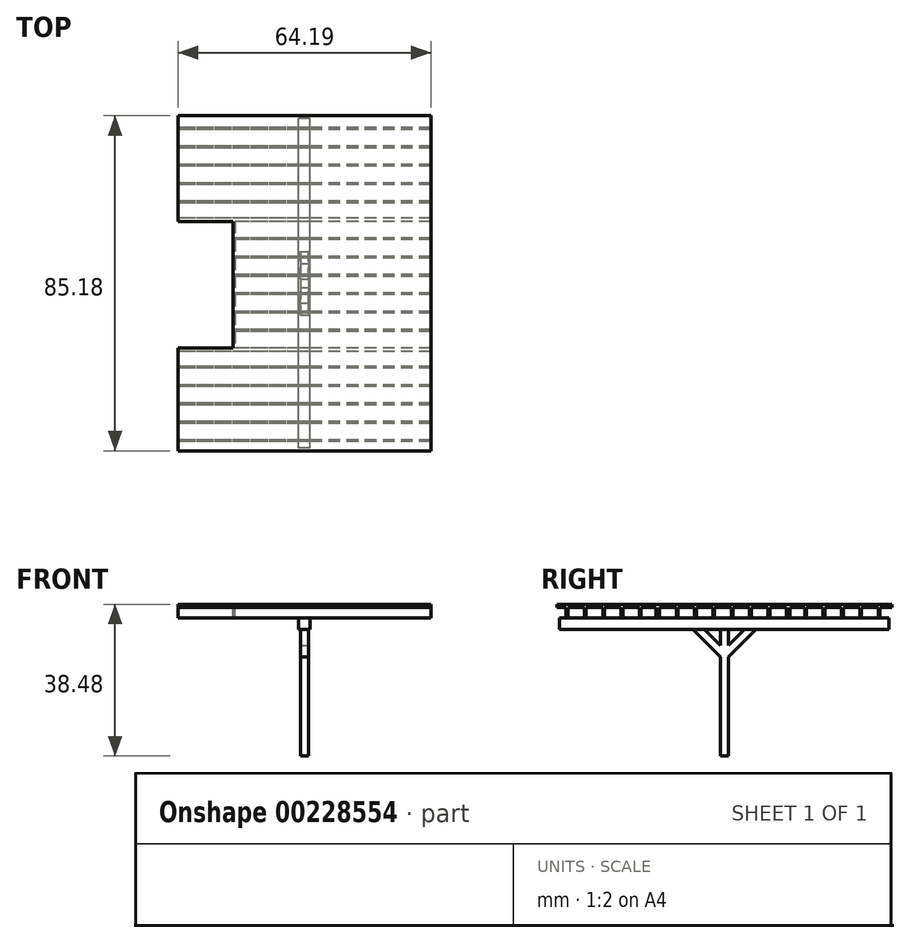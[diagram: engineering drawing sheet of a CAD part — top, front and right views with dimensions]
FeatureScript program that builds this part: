
annotation { "Feature Type Name" : "Feature", "Feature Type Description" : "" }
export const myFeature = defineFeature(function(context is Context, id is Id, definition is map)
    precondition{}
    {
        {
            var Q0;
            Q0=qCreatedBy(makeId("Top.planeOp"),FACE);
            var sketch = newSketch(context, id + "F0", { "sketchPlane" : qUnion([Q0])});
            skLineSegment(sketch, "E0.bottom", {"start": v(-4.2, 0) * mm, "end": v(5863.2, 0) * mm});
            skLineSegment(sketch, "E0.top", {"start": v(-4.2, -7696.2) * mm, "end": v(5863.2, -7696.2) * mm});
            skLineSegment(sketch, "E0.left", {"start": v(-4.2, 0) * mm, "end": v(-4.2, -7696.2) * mm});
            skLineSegment(sketch, "E0.right", {"start": v(5863.2, 0) * mm, "end": v(5863.2, -7696.2) * mm});
            skSolve(sketch);
        }
        {
            var Q0;
            Q0=makeQuery(id+"F0.imprint","IMPRINT",FACE,{"disambiguationData":[TD([[makeQuery(id+"F0.imprint","IMPRINT",EDGE,{"derivedFrom":sQuery(id+"F0.wireOp",EDGE,"E0.bottom")}),-1.0]])]});
            extrude(context, id + "F1", {"entities" : qUnion([Q0]), "depth" : 69.14 * mm});
        }
        {
            var Q0;
            Q0=makeQuery(id+"F1.opExtrude","CAP_FACE",FACE,{"disambiguationData":[OSD([sQuery(id+"F0.wireOp",EDGE,"E0.bottom"),sQuery(id+"F0.wireOp",EDGE,"E0.top"),sQuery(id+"F0.wireOp",EDGE,"E0.left"),sQuery(id+"F0.wireOp",EDGE,"E0.right")])],"isStart":true});
            var sketch = newSketch(context, id + "F2", { "sketchPlane" : qUnion([Q0])});
            skLineSegment(sketch, "E1.0", {"start": v(33.9, 7658.1) * mm, "end": v(5825.1, 7658.1) * mm});
            skLineSegment(sketch, "E1.1", {"start": v(33.9, 38.1) * mm, "end": v(33.9, 7658.1) * mm});
            skLineSegment(sketch, "E1.2", {"start": v(33.9, 38.1) * mm, "end": v(5825.1, 38.1) * mm});
            skLineSegment(sketch, "E1.3", {"start": v(5825.1, 38.1) * mm, "end": v(5825.1, 7658.1) * mm});
            skSolve(sketch);
        }
        {
            var Q0;
            Q0=makeQuery(id+"F2.imprint","IMPRINT",FACE,{"disambiguationData":[TD([[makeQuery(id+"F2.imprint","IMPRINT",EDGE,{"derivedFrom":sQuery(id+"F2.wireOp",EDGE,"E1.0")}),1.0]])]});
            extrude(context, id + "F3", {"entities" : qUnion([Q0]), "operationType" : NewBodyOperationType.ADD, "depth" : 234.95 * mm});
        }
        {
            var Q0;
            Q0=qCreatedBy(makeId("Right.planeOp"),FACE);
            var sketch = newSketch(context, id + "F4", { "sketchPlane" : qUnion([Q0])});
            skLineSegment(sketch, "E2.bottom", {"start": v(-406.4, 0) * mm, "end": v(-444.5, 0) * mm});
            skLineSegment(sketch, "E2.top", {"start": v(-406.4, -234.95) * mm, "end": v(-444.5, -234.95) * mm});
            skLineSegment(sketch, "E2.left", {"start": v(-406.4, 0) * mm, "end": v(-406.4, -234.95) * mm});
            skLineSegment(sketch, "E2.right", {"start": v(-444.5, 0) * mm, "end": v(-444.5, -234.95) * mm});
            skLineSegment(sketch, "E3.1.0.0", {"start": v(-812.8, 0) * mm, "end": v(-812.8, -234.95) * mm});
            skLineSegment(sketch, "E3.1.0.1", {"start": v(-850.9, 0) * mm, "end": v(-850.9, -234.95) * mm});
            skLineSegment(sketch, "E3.1.0.2", {"start": v(-812.8, 0) * mm, "end": v(-850.9, 0) * mm});
            skLineSegment(sketch, "E3.1.0.3", {"start": v(-812.8, -234.95) * mm, "end": v(-850.9, -234.95) * mm});
            skLineSegment(sketch, "E3.2.0.0", {"start": v(-1219.2, 0) * mm, "end": v(-1219.2, -234.95) * mm});
            skLineSegment(sketch, "E3.2.0.1", {"start": v(-1257.3, 0) * mm, "end": v(-1257.3, -234.95) * mm});
            skLineSegment(sketch, "E3.2.0.2", {"start": v(-1219.2, 0) * mm, "end": v(-1257.3, 0) * mm});
            skLineSegment(sketch, "E3.2.0.3", {"start": v(-1219.2, -234.95) * mm, "end": v(-1257.3, -234.95) * mm});
            skLineSegment(sketch, "E3.3.0.0", {"start": v(-1625.6, 0) * mm, "end": v(-1625.6, -234.95) * mm});
            skLineSegment(sketch, "E3.3.0.1", {"start": v(-1663.7, 0) * mm, "end": v(-1663.7, -234.95) * mm});
            skLineSegment(sketch, "E3.3.0.2", {"start": v(-1625.6, 0) * mm, "end": v(-1663.7, 0) * mm});
            skLineSegment(sketch, "E3.3.0.3", {"start": v(-1625.6, -234.95) * mm, "end": v(-1663.7, -234.95) * mm});
            skLineSegment(sketch, "E3.4.0.0", {"start": v(-2032, 0) * mm, "end": v(-2032, -234.95) * mm});
            skLineSegment(sketch, "E3.4.0.1", {"start": v(-2070.1, 0) * mm, "end": v(-2070.1, -234.95) * mm});
            skLineSegment(sketch, "E3.4.0.2", {"start": v(-2032, 0) * mm, "end": v(-2070.1, 0) * mm});
            skLineSegment(sketch, "E3.4.0.3", {"start": v(-2032, -234.95) * mm, "end": v(-2070.1, -234.95) * mm});
            skLineSegment(sketch, "E3.5.0.0", {"start": v(-2438.4, 0) * mm, "end": v(-2438.4, -234.95) * mm});
            skLineSegment(sketch, "E3.5.0.1", {"start": v(-2476.5, 0) * mm, "end": v(-2476.5, -234.95) * mm});
            skLineSegment(sketch, "E3.5.0.2", {"start": v(-2438.4, 0) * mm, "end": v(-2476.5, 0) * mm});
            skLineSegment(sketch, "E3.5.0.3", {"start": v(-2438.4, -234.95) * mm, "end": v(-2476.5, -234.95) * mm});
            skLineSegment(sketch, "E3.6.0.0", {"start": v(-2844.8, 0) * mm, "end": v(-2844.8, -234.95) * mm});
            skLineSegment(sketch, "E3.6.0.1", {"start": v(-2882.9, 0) * mm, "end": v(-2882.9, -234.95) * mm});
            skLineSegment(sketch, "E3.6.0.2", {"start": v(-2844.8, 0) * mm, "end": v(-2882.9, 0) * mm});
            skLineSegment(sketch, "E3.6.0.3", {"start": v(-2844.8, -234.95) * mm, "end": v(-2882.9, -234.95) * mm});
            skLineSegment(sketch, "E3.7.0.0", {"start": v(-3251.2, 0) * mm, "end": v(-3251.2, -234.95) * mm});
            skLineSegment(sketch, "E3.7.0.1", {"start": v(-3289.3, 0) * mm, "end": v(-3289.3, -234.95) * mm});
            skLineSegment(sketch, "E3.7.0.2", {"start": v(-3251.2, 0) * mm, "end": v(-3289.3, 0) * mm});
            skLineSegment(sketch, "E3.7.0.3", {"start": v(-3251.2, -234.95) * mm, "end": v(-3289.3, -234.95) * mm});
            skLineSegment(sketch, "E3.8.0.0", {"start": v(-3657.6, 0) * mm, "end": v(-3657.6, -234.95) * mm});
            skLineSegment(sketch, "E3.8.0.1", {"start": v(-3695.7, 0) * mm, "end": v(-3695.7, -234.95) * mm});
            skLineSegment(sketch, "E3.8.0.2", {"start": v(-3657.6, 0) * mm, "end": v(-3695.7, 0) * mm});
            skLineSegment(sketch, "E3.8.0.3", {"start": v(-3657.6, -234.95) * mm, "end": v(-3695.7, -234.95) * mm});
            skLineSegment(sketch, "E3.9.0.0", {"start": v(-4064, 0) * mm, "end": v(-4064, -234.95) * mm});
            skLineSegment(sketch, "E3.9.0.1", {"start": v(-4102.1, 0) * mm, "end": v(-4102.1, -234.95) * mm});
            skLineSegment(sketch, "E3.9.0.2", {"start": v(-4064, 0) * mm, "end": v(-4102.1, 0) * mm});
            skLineSegment(sketch, "E3.9.0.3", {"start": v(-4064, -234.95) * mm, "end": v(-4102.1, -234.95) * mm});
            skLineSegment(sketch, "E3.10.0.0", {"start": v(-4470.4, 0) * mm, "end": v(-4470.4, -234.95) * mm});
            skLineSegment(sketch, "E3.10.0.1", {"start": v(-4508.5, 0) * mm, "end": v(-4508.5, -234.95) * mm});
            skLineSegment(sketch, "E3.10.0.2", {"start": v(-4470.4, 0) * mm, "end": v(-4508.5, 0) * mm});
            skLineSegment(sketch, "E3.10.0.3", {"start": v(-4470.4, -234.95) * mm, "end": v(-4508.5, -234.95) * mm});
            skLineSegment(sketch, "E3.11.0.0", {"start": v(-4876.8, 0) * mm, "end": v(-4876.8, -234.95) * mm});
            skLineSegment(sketch, "E3.11.0.1", {"start": v(-4914.9, 0) * mm, "end": v(-4914.9, -234.95) * mm});
            skLineSegment(sketch, "E3.11.0.2", {"start": v(-4876.8, 0) * mm, "end": v(-4914.9, 0) * mm});
            skLineSegment(sketch, "E3.11.0.3", {"start": v(-4876.8, -234.95) * mm, "end": v(-4914.9, -234.95) * mm});
            skLineSegment(sketch, "E3.12.0.0", {"start": v(-5283.2, 0) * mm, "end": v(-5283.2, -234.95) * mm});
            skLineSegment(sketch, "E3.12.0.1", {"start": v(-5321.3, 0) * mm, "end": v(-5321.3, -234.95) * mm});
            skLineSegment(sketch, "E3.12.0.2", {"start": v(-5283.2, 0) * mm, "end": v(-5321.3, 0) * mm});
            skLineSegment(sketch, "E3.12.0.3", {"start": v(-5283.2, -234.95) * mm, "end": v(-5321.3, -234.95) * mm});
            skLineSegment(sketch, "E3.13.0.0", {"start": v(-5689.6, 0) * mm, "end": v(-5689.6, -234.95) * mm});
            skLineSegment(sketch, "E3.13.0.1", {"start": v(-5727.7, 0) * mm, "end": v(-5727.7, -234.95) * mm});
            skLineSegment(sketch, "E3.13.0.2", {"start": v(-5689.6, 0) * mm, "end": v(-5727.7, 0) * mm});
            skLineSegment(sketch, "E3.13.0.3", {"start": v(-5689.6, -234.95) * mm, "end": v(-5727.7, -234.95) * mm});
            skLineSegment(sketch, "E3.14.0.0", {"start": v(-6096, 0) * mm, "end": v(-6096, -234.95) * mm});
            skLineSegment(sketch, "E3.14.0.1", {"start": v(-6134.1, 0) * mm, "end": v(-6134.1, -234.95) * mm});
            skLineSegment(sketch, "E3.14.0.2", {"start": v(-6096, 0) * mm, "end": v(-6134.1, 0) * mm});
            skLineSegment(sketch, "E3.14.0.3", {"start": v(-6096, -234.95) * mm, "end": v(-6134.1, -234.95) * mm});
            skLineSegment(sketch, "E3.15.0.0", {"start": v(-6502.4, 0) * mm, "end": v(-6502.4, -234.95) * mm});
            skLineSegment(sketch, "E3.15.0.1", {"start": v(-6540.5, 0) * mm, "end": v(-6540.5, -234.95) * mm});
            skLineSegment(sketch, "E3.15.0.2", {"start": v(-6502.4, 0) * mm, "end": v(-6540.5, 0) * mm});
            skLineSegment(sketch, "E3.15.0.3", {"start": v(-6502.4, -234.95) * mm, "end": v(-6540.5, -234.95) * mm});
            skLineSegment(sketch, "E3.16.0.0", {"start": v(-6908.8, 0) * mm, "end": v(-6908.8, -234.95) * mm});
            skLineSegment(sketch, "E3.16.0.1", {"start": v(-6946.9, 0) * mm, "end": v(-6946.9, -234.95) * mm});
            skLineSegment(sketch, "E3.16.0.2", {"start": v(-6908.8, 0) * mm, "end": v(-6946.9, 0) * mm});
            skLineSegment(sketch, "E3.16.0.3", {"start": v(-6908.8, -234.95) * mm, "end": v(-6946.9, -234.95) * mm});
            skLineSegment(sketch, "E3.direction1", {"start": v(-444.5, -234.95) * mm, "end": v(-850.9, -234.95) * mm, "construction": true});
            skLineSegment(sketch, "E4.0.17.0", {"start": v(-7315.2, 0) * mm, "end": v(-7315.2, -234.95) * mm});
            skLineSegment(sketch, "E4.3.17.0", {"start": v(-7353.3, 0) * mm, "end": v(-7353.3, -234.95) * mm});
            skLineSegment(sketch, "E4.6.17.0", {"start": v(-7315.2, 0) * mm, "end": v(-7353.3, 0) * mm});
            skLineSegment(sketch, "E4.9.17.0", {"start": v(-7315.2, -234.95) * mm, "end": v(-7353.3, -234.95) * mm});
            skSolve(sketch);
        }
        {
            var Q0;
            Q0=makeQuery(id+"F4.imprint","IMPRINT",FACE,{"disambiguationData":[TD([[makeQuery(id+"F4.imprint","IMPRINT",EDGE,{"derivedFrom":sQuery(id+"F4.wireOp",EDGE,"E2.bottom")}),1.0]])]});
            var Q1;
            Q1=makeQuery(id+"F4.imprint","IMPRINT",FACE,{"disambiguationData":[TD([[makeQuery(id+"F4.imprint","IMPRINT",EDGE,{"derivedFrom":sQuery(id+"F4.wireOp",EDGE,"E3.1.0.0")}),-1.0]])]});
            var Q2;
            Q2=makeQuery(id+"F4.imprint","IMPRINT",FACE,{"disambiguationData":[TD([[makeQuery(id+"F4.imprint","IMPRINT",EDGE,{"derivedFrom":sQuery(id+"F4.wireOp",EDGE,"E3.2.0.0")}),-1.0]])]});
            var Q3;
            Q3=makeQuery(id+"F4.imprint","IMPRINT",FACE,{"disambiguationData":[TD([[makeQuery(id+"F4.imprint","IMPRINT",EDGE,{"derivedFrom":sQuery(id+"F4.wireOp",EDGE,"E3.3.0.0")}),-1.0]])]});
            var Q4;
            Q4=makeQuery(id+"F4.imprint","IMPRINT",FACE,{"disambiguationData":[TD([[makeQuery(id+"F4.imprint","IMPRINT",EDGE,{"derivedFrom":sQuery(id+"F4.wireOp",EDGE,"E3.4.0.0")}),-1.0]])]});
            var Q5;
            Q5=makeQuery(id+"F4.imprint","IMPRINT",FACE,{"disambiguationData":[TD([[makeQuery(id+"F4.imprint","IMPRINT",EDGE,{"derivedFrom":sQuery(id+"F4.wireOp",EDGE,"E3.5.0.0")}),-1.0]])]});
            var Q6;
            Q6=makeQuery(id+"F4.imprint","IMPRINT",FACE,{"disambiguationData":[TD([[makeQuery(id+"F4.imprint","IMPRINT",EDGE,{"derivedFrom":sQuery(id+"F4.wireOp",EDGE,"E3.6.0.0")}),-1.0]])]});
            var Q7;
            Q7=makeQuery(id+"F4.imprint","IMPRINT",FACE,{"disambiguationData":[TD([[makeQuery(id+"F4.imprint","IMPRINT",EDGE,{"derivedFrom":sQuery(id+"F4.wireOp",EDGE,"E3.7.0.0")}),-1.0]])]});
            var Q8;
            Q8=makeQuery(id+"F4.imprint","IMPRINT",FACE,{"disambiguationData":[TD([[makeQuery(id+"F4.imprint","IMPRINT",EDGE,{"derivedFrom":sQuery(id+"F4.wireOp",EDGE,"E3.8.0.0")}),-1.0]])]});
            var Q9;
            Q9=makeQuery(id+"F4.imprint","IMPRINT",FACE,{"disambiguationData":[TD([[makeQuery(id+"F4.imprint","IMPRINT",EDGE,{"derivedFrom":sQuery(id+"F4.wireOp",EDGE,"E3.9.0.0")}),-1.0]])]});
            var Q10;
            Q10=makeQuery(id+"F4.imprint","IMPRINT",FACE,{"disambiguationData":[TD([[makeQuery(id+"F4.imprint","IMPRINT",EDGE,{"derivedFrom":sQuery(id+"F4.wireOp",EDGE,"E3.10.0.0")}),-1.0]])]});
            var Q11;
            Q11=makeQuery(id+"F4.imprint","IMPRINT",FACE,{"disambiguationData":[TD([[makeQuery(id+"F4.imprint","IMPRINT",EDGE,{"derivedFrom":sQuery(id+"F4.wireOp",EDGE,"E3.11.0.0")}),-1.0]])]});
            var Q12;
            Q12=makeQuery(id+"F4.imprint","IMPRINT",FACE,{"disambiguationData":[TD([[makeQuery(id+"F4.imprint","IMPRINT",EDGE,{"derivedFrom":sQuery(id+"F4.wireOp",EDGE,"E3.12.0.0")}),-1.0]])]});
            var Q13;
            Q13=makeQuery(id+"F4.imprint","IMPRINT",FACE,{"disambiguationData":[TD([[makeQuery(id+"F4.imprint","IMPRINT",EDGE,{"derivedFrom":sQuery(id+"F4.wireOp",EDGE,"E3.13.0.0")}),-1.0]])]});
            var Q14;
            Q14=makeQuery(id+"F4.imprint","IMPRINT",FACE,{"disambiguationData":[TD([[makeQuery(id+"F4.imprint","IMPRINT",EDGE,{"derivedFrom":sQuery(id+"F4.wireOp",EDGE,"E3.14.0.0")}),-1.0]])]});
            var Q15;
            Q15=makeQuery(id+"F4.imprint","IMPRINT",FACE,{"disambiguationData":[TD([[makeQuery(id+"F4.imprint","IMPRINT",EDGE,{"derivedFrom":sQuery(id+"F4.wireOp",EDGE,"E3.15.0.0")}),-1.0]])]});
            var Q16;
            Q16=makeQuery(id+"F4.imprint","IMPRINT",FACE,{"disambiguationData":[TD([[makeQuery(id+"F4.imprint","IMPRINT",EDGE,{"derivedFrom":sQuery(id+"F4.wireOp",EDGE,"E3.16.0.0")}),-1.0]])]});
            var Q17;
            Q17=makeQuery(id+"F4.imprint","IMPRINT",FACE,{"disambiguationData":[TD([[makeQuery(id+"F4.imprint","IMPRINT",EDGE,{"derivedFrom":sQuery(id+"F4.wireOp",EDGE,"E4.0.17.0")}),-1.0]])]});
            var Q18;
            Q18=makeQuery(id+"F1.opExtrude","SWEPT_FACE",FACE,{"disambiguationData":[OSD([sQuery(id+"F0.wireOp",EDGE,"E0.right")])]});
            extrude(context, id + "F5", {"entities" : qUnion([Q0, Q1, Q2, Q3, Q4, Q5, Q6, Q7, Q8, Q9, Q10, Q11, Q12, Q13, Q14, Q15, Q16, Q17]), "operationType" : NewBodyOperationType.ADD, "endBound" : BoundingType.UP_TO_SURFACE, "endBoundEntityFace" : qUnion([Q18]), "depth" : 25.4 * mm});
        }
        {
            var Q0;
            {var subQ0=sQuery(id+"F0.wireOp",EDGE,"E0.bottom");Q0=makeQuery(id+"F3.boolean.opBoolean","MERGE",FACE,{"derivedFrom":[makeQuery(id+"F1.opExtrude","SWEPT_FACE",FACE,{"disambiguationData":[OSD([subQ0])]}),makeQuery(id+"F3.opExtrude","SWEPT_FACE",FACE,{"disambiguationData":[OSD([subQ0])]})]});}
            cPlane(context, id + "F6", {"entities" : qUnion([Q0]), "cplaneType" : CPlaneType.OFFSET, "offset" : 203.2 * mm, "oppositeDirection" : true, "width" : 152.4 * mm, "height" : 152.4 * mm});
        }
        {
            var Q0;
            Q0=qCreatedBy(id+"F6.planeOp",FACE);
            var sketch = newSketch(context, id + "F7", { "sketchPlane" : qUnion([Q0])});
            skLineSegment(sketch, "E5.bottom", {"start": v(-3056.5, -234.95) * mm, "end": v(-2802.5, -234.95) * mm});
            skLineSegment(sketch, "E5.top", {"start": v(-3056.5, -488.95) * mm, "end": v(-2802.5, -488.95) * mm});
            skLineSegment(sketch, "E5.left", {"start": v(-3056.5, -234.95) * mm, "end": v(-3056.5, -488.95) * mm});
            skLineSegment(sketch, "E5.right", {"start": v(-2802.5, -234.95) * mm, "end": v(-2802.5, -488.95) * mm});
            skSolve(sketch);
        }
        {
            var Q0;
            Q0=makeQuery(id+"F7.imprint","IMPRINT",FACE,{"disambiguationData":[TD([[makeQuery(id+"F7.imprint","IMPRINT",EDGE,{"derivedFrom":sQuery(id+"F7.wireOp",EDGE,"E5.bottom")}),-1.0]])]});
            extrude(context, id + "F8", {"entities" : qUnion([Q0]), "operationType" : NewBodyOperationType.ADD, "oppositeDirection" : true, "depth" : 7289.8 * mm});
        }
        {
            var Q0;
            Q0=makeQuery(id+"F8.opExtrude","SWEPT_FACE",FACE,{"disambiguationData":[OSD([sQuery(id+"F7.wireOp",EDGE,"E5.top")])]});
            var sketch = newSketch(context, id + "F9", { "sketchPlane" : qUnion([Q0])});
            skLineSegment(sketch, "E6", {"start": v(2929.5, 7493) * mm, "end": v(2929.5, 203.2) * mm, "construction": true});
            skLineSegment(sketch, "E7", {"start": v(2802.5, 3848.1) * mm, "end": v(3056.5, 3848.1) * mm, "construction": true});
            skLineSegment(sketch, "E8.bottom", {"start": v(3021.58, 3756.03) * mm, "end": v(2837.43, 3756.03) * mm});
            skLineSegment(sketch, "E8.top", {"start": v(3021.58, 3940.18) * mm, "end": v(2837.43, 3940.18) * mm});
            skLineSegment(sketch, "E8.left", {"start": v(3021.58, 3756.03) * mm, "end": v(3021.58, 3940.18) * mm});
            skLineSegment(sketch, "E8.right", {"start": v(2837.43, 3756.03) * mm, "end": v(2837.43, 3940.18) * mm});
            skPoint(sketch, "E8.middle", {"position": v(2929.5, 3848.1) * mm});
            skSolve(sketch);
        }
        {
            var Q0;
            Q0=makeQuery(id+"F9.imprint","IMPRINT",FACE,{"disambiguationData":[TD([[makeQuery(id+"F9.imprint","IMPRINT",EDGE,{"derivedFrom":sQuery(id+"F9.wireOp",EDGE,"E8.bottom")}),-1.0]])]});
            extrude(context, id + "F10", {"entities" : qUnion([Q0]), "operationType" : NewBodyOperationType.ADD, "depth" : 2794 * mm});
        }
        {
            var Q0;
            Q0=makeQuery(id+"F10.opExtrude","SWEPT_FACE",FACE,{"disambiguationData":[OSD([sQuery(id+"F9.wireOp",EDGE,"E8.left")])]});
            var sketch = newSketch(context, id + "F11", { "sketchPlane" : qUnion([Q0])});
            skLineSegment(sketch, "E9", {"start": v(-4289.35, -488.95) * mm, "end": v(-3940.17, -838.12) * mm});
            skLineSegment(sketch, "E10", {"start": v(-3940.17, -838.12) * mm, "end": v(-3940.17, -1098.55) * mm});
            skLineSegment(sketch, "E11", {"start": v(-3940.17, -1098.55) * mm, "end": v(-4549.77, -488.95) * mm});
            skLineSegment(sketch, "E12", {"start": v(-4549.77, -488.95) * mm, "end": v(-4289.35, -488.95) * mm});
            skLineSegment(sketch, "E13", {"start": v(-3848.1, -488.95) * mm, "end": v(-3848.1, -1270.1) * mm, "construction": true});
            skLineSegment(sketch, "E14.MirrorCS", {"start": v(-3146.42, -488.95) * mm, "end": v(-3406.85, -488.95) * mm});
            skLineSegment(sketch, "E15.MirrorCS", {"start": v(-3756.02, -1098.55) * mm, "end": v(-3146.42, -488.95) * mm});
            skLineSegment(sketch, "E16.MirrorCS", {"start": v(-3406.85, -488.95) * mm, "end": v(-3756.02, -838.12) * mm});
            skLineSegment(sketch, "E17.MirrorCS", {"start": v(-3756.02, -838.12) * mm, "end": v(-3756.02, -1098.55) * mm});
            skSolve(sketch);
        }
        {
            var Q0;
            Q0=makeQuery(id+"F11.imprint","IMPRINT",FACE,{"disambiguationData":[TD([[makeQuery(id+"F11.imprint","IMPRINT",EDGE,{"derivedFrom":sQuery(id+"F11.wireOp",EDGE,"E9")}),-1.0]])]});
            var Q1;
            Q1=makeQuery(id+"F11.imprint","IMPRINT",FACE,{"disambiguationData":[TD([[makeQuery(id+"F11.imprint","IMPRINT",EDGE,{"derivedFrom":sQuery(id+"F11.wireOp",EDGE,"E14.MirrorCS")}),1.0]])]});
            var Q2;
            Q2=makeQuery(id+"F10.opExtrude","SWEPT_FACE",FACE,{"disambiguationData":[OSD([sQuery(id+"F9.wireOp",EDGE,"E8.right")])]});
            extrude(context, id + "F12", {"entities" : qUnion([Q0, Q1]), "operationType" : NewBodyOperationType.ADD, "endBound" : BoundingType.UP_TO_SURFACE, "oppositeDirection" : true, "endBoundEntityFace" : qUnion([Q2]), "depth" : 25.4 * mm});
        }
        {
            var Q0;
            Q0=makeQuery(id+"F1.opExtrude","CAP_FACE",FACE,{"disambiguationData":[OSD([sQuery(id+"F0.wireOp",EDGE,"E0.bottom"),sQuery(id+"F0.wireOp",EDGE,"E0.top"),sQuery(id+"F0.wireOp",EDGE,"E0.left"),sQuery(id+"F0.wireOp",EDGE,"E0.right")])],"isStart":false});
            var sketch = newSketch(context, id + "F13", { "sketchPlane" : qUnion([Q0])});
            skLineSegment(sketch, "E18.0", {"start": v(134.08, -138.28) * mm, "end": v(5724.93, -138.28) * mm});
            skLineSegment(sketch, "E18.1", {"start": v(134.08, -138.28) * mm, "end": v(134.08, -7557.92) * mm});
            skLineSegment(sketch, "E18.2", {"start": v(134.08, -7557.92) * mm, "end": v(5724.93, -7557.92) * mm});
            skLineSegment(sketch, "E18.3", {"start": v(5724.93, -138.28) * mm, "end": v(5724.93, -7557.92) * mm});
            skLineSegment(sketch, "E19.0", {"start": v(-4.2, 0) * mm, "end": v(5863.2, 0) * mm});
            skLineSegment(sketch, "E20.0", {"start": v(-4.2, 0) * mm, "end": v(-4.2, -7696.2) * mm});
            skLineSegment(sketch, "E21.0", {"start": v(-4.2, -7696.2) * mm, "end": v(5863.2, -7696.2) * mm});
            skLineSegment(sketch, "E22.0", {"start": v(5863.2, 0) * mm, "end": v(5863.2, -7696.2) * mm});
            skSolve(sketch);
        }
        {
            var Q0;
            Q0=makeQuery(id+"F13.imprint","IMPRINT",FACE,{"disambiguationData":[TD([[makeQuery(id+"F13.imprint","IMPRINT",EDGE,{"derivedFrom":sQuery(id+"F13.wireOp",EDGE,"E18.0")}),1.0]])]});
            var Q1;
            Q1=makeQuery(id+"F5.boolean.opBoolean","MERGE",FACE,{"derivedFrom":[makeQuery(id+"F3.opExtrude","CAP_FACE",FACE,{"disambiguationData":[OSD([sQuery(id+"F0.wireOp",EDGE,"E0.bottom"),sQuery(id+"F0.wireOp",EDGE,"E0.top"),sQuery(id+"F0.wireOp",EDGE,"E0.left"),sQuery(id+"F0.wireOp",EDGE,"E0.right"),sQuery(id+"F2.wireOp",EDGE,"E1.0"),sQuery(id+"F2.wireOp",EDGE,"E1.1"),sQuery(id+"F2.wireOp",EDGE,"E1.2"),sQuery(id+"F2.wireOp",EDGE,"E1.3")])],"isStart":false}),makeQuery(id+"F5.opExtrude","SWEPT_FACE",FACE,{"disambiguationData":[OSD([sQuery(id+"F4.wireOp",EDGE,"E2.top")])]}),makeQuery(id+"F5.opExtrude","SWEPT_FACE",FACE,{"disambiguationData":[OSD([sQuery(id+"F4.wireOp",EDGE,"E3.1.0.3")])]}),makeQuery(id+"F5.opExtrude","SWEPT_FACE",FACE,{"disambiguationData":[OSD([sQuery(id+"F4.wireOp",EDGE,"E3.2.0.3")])]}),makeQuery(id+"F5.opExtrude","SWEPT_FACE",FACE,{"disambiguationData":[OSD([sQuery(id+"F4.wireOp",EDGE,"E3.3.0.3")])]}),makeQuery(id+"F5.opExtrude","SWEPT_FACE",FACE,{"disambiguationData":[OSD([sQuery(id+"F4.wireOp",EDGE,"E3.4.0.3")])]}),makeQuery(id+"F5.opExtrude","SWEPT_FACE",FACE,{"disambiguationData":[OSD([sQuery(id+"F4.wireOp",EDGE,"E3.5.0.3")])]}),makeQuery(id+"F5.opExtrude","SWEPT_FACE",FACE,{"disambiguationData":[OSD([sQuery(id+"F4.wireOp",EDGE,"E3.6.0.3")])]}),makeQuery(id+"F5.opExtrude","SWEPT_FACE",FACE,{"disambiguationData":[OSD([sQuery(id+"F4.wireOp",EDGE,"E3.7.0.3")])]}),makeQuery(id+"F5.opExtrude","SWEPT_FACE",FACE,{"disambiguationData":[OSD([sQuery(id+"F4.wireOp",EDGE,"E3.8.0.3")])]}),makeQuery(id+"F5.opExtrude","SWEPT_FACE",FACE,{"disambiguationData":[OSD([sQuery(id+"F4.wireOp",EDGE,"E3.9.0.3")])]}),makeQuery(id+"F5.opExtrude","SWEPT_FACE",FACE,{"disambiguationData":[OSD([sQuery(id+"F4.wireOp",EDGE,"E3.10.0.3")])]}),makeQuery(id+"F5.opExtrude","SWEPT_FACE",FACE,{"disambiguationData":[OSD([sQuery(id+"F4.wireOp",EDGE,"E3.11.0.3")])]}),makeQuery(id+"F5.opExtrude","SWEPT_FACE",FACE,{"disambiguationData":[OSD([sQuery(id+"F4.wireOp",EDGE,"E3.12.0.3")])]}),makeQuery(id+"F5.opExtrude","SWEPT_FACE",FACE,{"disambiguationData":[OSD([sQuery(id+"F4.wireOp",EDGE,"E3.13.0.3")])]}),makeQuery(id+"F5.opExtrude","SWEPT_FACE",FACE,{"disambiguationData":[OSD([sQuery(id+"F4.wireOp",EDGE,"E3.14.0.3")])]}),makeQuery(id+"F5.opExtrude","SWEPT_FACE",FACE,{"disambiguationData":[OSD([sQuery(id+"F4.wireOp",EDGE,"E3.15.0.3")])]}),makeQuery(id+"F5.opExtrude","SWEPT_FACE",FACE,{"disambiguationData":[OSD([sQuery(id+"F4.wireOp",EDGE,"E3.16.0.3")])]}),makeQuery(id+"F5.opExtrude","SWEPT_FACE",FACE,{"disambiguationData":[OSD([sQuery(id+"F4.wireOp",EDGE,"E4.9.17.0")])]})]});
            extrude(context, id + "F14", {"entities" : qUnion([Q0]), "operationType" : NewBodyOperationType.REMOVE, "endBound" : BoundingType.UP_TO_SURFACE, "oppositeDirection" : true, "endBoundEntityFace" : qUnion([Q1]), "depth" : 25.4 * mm});
        }
        {
            var Q0;
            Q0=makeQuery(id+"F1.opExtrude","CAP_FACE",FACE,{"disambiguationData":[OSD([sQuery(id+"F0.wireOp",EDGE,"E0.bottom"),sQuery(id+"F0.wireOp",EDGE,"E0.top"),sQuery(id+"F0.wireOp",EDGE,"E0.left"),sQuery(id+"F0.wireOp",EDGE,"E0.right")])],"isStart":false});
            var sketch = newSketch(context, id + "F15", { "sketchPlane" : qUnion([Q0])});
            skLineSegment(sketch, "E23.bottom", {"start": v(134.08, -2476.5) * mm, "end": v(1353.28, -2476.5) * mm});
            skLineSegment(sketch, "E23.top", {"start": v(134.08, -5283.2) * mm, "end": v(1353.28, -5283.2) * mm});
            skLineSegment(sketch, "E23.left", {"start": v(134.08, -2476.5) * mm, "end": v(134.08, -5283.2) * mm});
            skLineSegment(sketch, "E23.right", {"start": v(1353.28, -2476.5) * mm, "end": v(1353.28, -5283.2) * mm});
            skSolve(sketch);
        }
        {
            var Q0;
            Q0=makeQuery(id+"F15.imprint","IMPRINT",FACE,{"disambiguationData":[TD([[makeQuery(id+"F15.imprint","IMPRINT",EDGE,{"derivedFrom":sQuery(id+"F15.wireOp",EDGE,"E23.bottom")}),-1.0]])]});
            extrude(context, id + "F16", {"entities" : qUnion([Q0]), "operationType" : NewBodyOperationType.REMOVE, "oppositeDirection" : true, "depth" : 304.8 * mm});
        }
        {
            var Q0;
            Q0=makeQuery(id+"F16.boolean.opBoolean","COPY",FACE,{"derivedFrom":makeQuery(id+"F16.opExtrude","SWEPT_FACE",FACE,{"disambiguationData":[OSD([sQuery(id+"F15.wireOp",EDGE,"E23.right")])]})});
            var sketch = newSketch(context, id + "F17", { "sketchPlane" : qUnion([Q0])});
            skLineSegment(sketch, "E24.bottom", {"start": v(2476.5, 0) * mm, "end": v(5283.2, 0) * mm});
            skLineSegment(sketch, "E24.top", {"start": v(2476.5, -234.95) * mm, "end": v(5283.2, -234.95) * mm});
            skLineSegment(sketch, "E24.left", {"start": v(2476.5, 0) * mm, "end": v(2476.5, -234.95) * mm});
            skLineSegment(sketch, "E24.right", {"start": v(5283.2, 0) * mm, "end": v(5283.2, -234.95) * mm});
            skSolve(sketch);
        }
        {
            var Q0;
            {var subQ0=sQuery(id+"F17.wireOp",EDGE,"E24.left");Q0=makeQuery(id+"F17.imprint","IMPRINT",FACE,{"disambiguationData":[TD([[makeQuery(id+"F17.imprint","IMPRINT",EDGE,{"derivedFrom":subQ0}),1.0]])]});}
            var Q1;
            {var subQ1=makeQuery(id+"F16.opExtrude","SWEPT_FACE",FACE,{"disambiguationData":[OSD([sQuery(id+"F15.wireOp",EDGE,"E23.right")])]});var subQ2=makeQuery(id+"F16.boolean.opBoolean","INTERSECT",EDGE,{"derivedFrom":[makeQuery(id+"F5.opExtrude","SWEPT_FACE",FACE,{"disambiguationData":[OSD([sQuery(id+"F4.wireOp",EDGE,"E3.6.0.1")])]}),subQ1]});Q1=makeQuery(id+"F17.imprint","IMPRINT",FACE,{"disambiguationData":[TD([[makeQuery(id+"F17.imprint","IMPRINT",EDGE,{"derivedFrom":subQ2}),-1.0]])]});}
            var Q2;
            {var subQ1=makeQuery(id+"F16.opExtrude","SWEPT_FACE",FACE,{"disambiguationData":[OSD([sQuery(id+"F15.wireOp",EDGE,"E23.right")])]});var subQ2=makeQuery(id+"F16.boolean.opBoolean","INTERSECT",EDGE,{"derivedFrom":[makeQuery(id+"F5.opExtrude","SWEPT_FACE",FACE,{"disambiguationData":[OSD([sQuery(id+"F4.wireOp",EDGE,"E3.7.0.1")])]}),subQ1]});Q2=makeQuery(id+"F17.imprint","IMPRINT",FACE,{"disambiguationData":[TD([[makeQuery(id+"F17.imprint","IMPRINT",EDGE,{"derivedFrom":subQ2}),-1.0]])]});}
            var Q3;
            {var subQ1=makeQuery(id+"F16.opExtrude","SWEPT_FACE",FACE,{"disambiguationData":[OSD([sQuery(id+"F15.wireOp",EDGE,"E23.right")])]});var subQ2=makeQuery(id+"F16.boolean.opBoolean","INTERSECT",EDGE,{"derivedFrom":[makeQuery(id+"F5.opExtrude","SWEPT_FACE",FACE,{"disambiguationData":[OSD([sQuery(id+"F4.wireOp",EDGE,"E3.8.0.1")])]}),subQ1]});Q3=makeQuery(id+"F17.imprint","IMPRINT",FACE,{"disambiguationData":[TD([[makeQuery(id+"F17.imprint","IMPRINT",EDGE,{"derivedFrom":subQ2}),-1.0]])]});}
            var Q4;
            {var subQ1=makeQuery(id+"F16.opExtrude","SWEPT_FACE",FACE,{"disambiguationData":[OSD([sQuery(id+"F15.wireOp",EDGE,"E23.right")])]});var subQ2=makeQuery(id+"F16.boolean.opBoolean","INTERSECT",EDGE,{"derivedFrom":[makeQuery(id+"F5.opExtrude","SWEPT_FACE",FACE,{"disambiguationData":[OSD([sQuery(id+"F4.wireOp",EDGE,"E3.9.0.1")])]}),subQ1]});Q4=makeQuery(id+"F17.imprint","IMPRINT",FACE,{"disambiguationData":[TD([[makeQuery(id+"F17.imprint","IMPRINT",EDGE,{"derivedFrom":subQ2}),-1.0]])]});}
            var Q5;
            {var subQ1=makeQuery(id+"F16.opExtrude","SWEPT_FACE",FACE,{"disambiguationData":[OSD([sQuery(id+"F15.wireOp",EDGE,"E23.right")])]});var subQ2=makeQuery(id+"F16.boolean.opBoolean","INTERSECT",EDGE,{"derivedFrom":[makeQuery(id+"F5.opExtrude","SWEPT_FACE",FACE,{"disambiguationData":[OSD([sQuery(id+"F4.wireOp",EDGE,"E3.10.0.1")])]}),subQ1]});Q5=makeQuery(id+"F17.imprint","IMPRINT",FACE,{"disambiguationData":[TD([[makeQuery(id+"F17.imprint","IMPRINT",EDGE,{"derivedFrom":subQ2}),-1.0]])]});}
            var Q6;
            {var subQ0=sQuery(id+"F17.wireOp",EDGE,"E24.right");Q6=makeQuery(id+"F17.imprint","IMPRINT",FACE,{"disambiguationData":[TD([[makeQuery(id+"F17.imprint","IMPRINT",EDGE,{"derivedFrom":subQ0}),-1.0]])]});}
            extrude(context, id + "F18", {"entities" : qUnion([Q0, Q1, Q2, Q3, Q4, Q5, Q6]), "operationType" : NewBodyOperationType.ADD, "oppositeDirection" : true, "depth" : 38.1 * mm});
        }
        {
            var Q0;
            Q0=makeQuery(id+"F5.opExtrude","SWEPT_FACE",FACE,{"disambiguationData":[OSD([sQuery(id+"F4.wireOp",EDGE,"E3.12.0.1")])]});
            extrude(context, id + "F19", {"entities" : qUnion([Q0]), "operationType" : NewBodyOperationType.ADD, "depth" : 38.1 * mm});
        }
        {
            var Q0;
            Q0=makeQuery(id+"F5.opExtrude","SWEPT_FACE",FACE,{"disambiguationData":[OSD([sQuery(id+"F4.wireOp",EDGE,"E3.5.0.0")])]});
            extrude(context, id + "F20", {"entities" : qUnion([Q0]), "operationType" : NewBodyOperationType.ADD, "depth" : 38.1 * mm});
        }
        {
            var Q0;
            Q0=makeQuery(id+"F1.opExtrude","SWEPT_BODY",BODY,{"disambiguationData":[OSD([sQuery(id+"F0.wireOp",EDGE,"E0.bottom"),sQuery(id+"F0.wireOp",EDGE,"E0.top"),sQuery(id+"F0.wireOp",EDGE,"E0.left"),sQuery(id+"F0.wireOp",EDGE,"E0.right")])]});
            var Q1;
            Q1=qCreatedBy(makeId("Origin.pointOp"),VERTEX);
            transform(context, id + "F21", {"entities" : qUnion([Q0]), "transformType" : TransformType.SCALE_UNIFORMLY, "scale" : 1 / 87.1, "scalePoint" : qUnion([Q1]), "makeCopy" : false});
        }
    });
